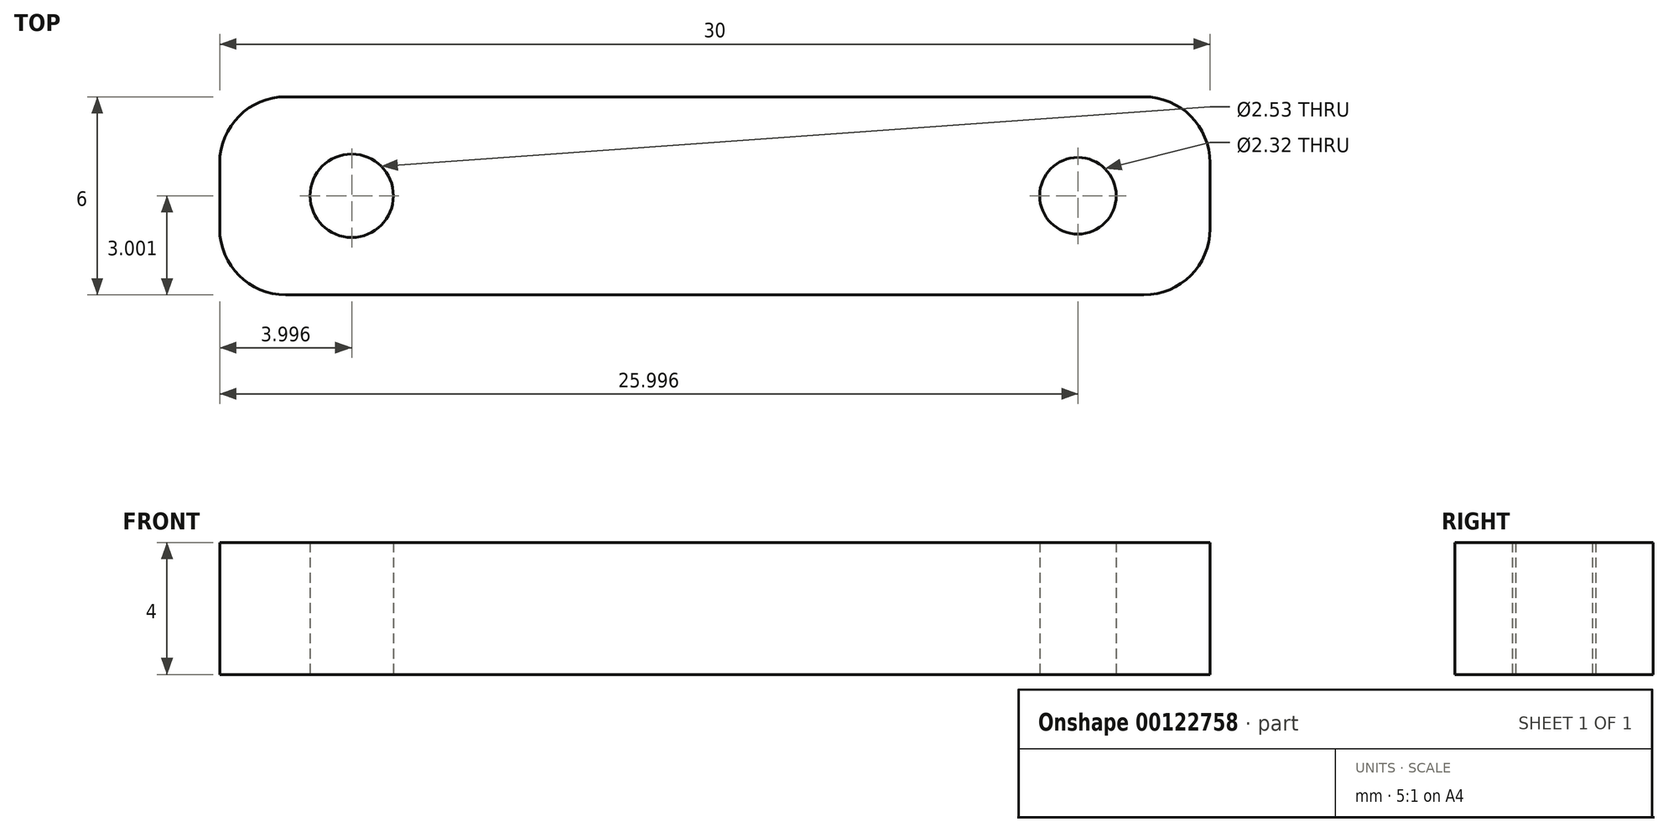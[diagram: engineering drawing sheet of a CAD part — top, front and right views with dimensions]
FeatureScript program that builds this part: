
annotation { "Feature Type Name" : "Feature", "Feature Type Description" : "" }
export const myFeature = defineFeature(function(context is Context, id is Id, definition is map)
    precondition{}
    {
        {
            var Q0;
            Q0=qCreatedBy(makeId("Top.planeOp"),FACE);
            var sketch = newSketch(context, id + "F0", { "sketchPlane" : qUnion([Q0])});
            skLineSegment(sketch, "E0.bottom", {"start": v(-1.74, 5.3) * mm, "end": v(24.26, 5.3) * mm});
            skLineSegment(sketch, "E0.top", {"start": v(-1.74, -0.7) * mm, "end": v(24.26, -0.7) * mm});
            skLineSegment(sketch, "E0.left", {"start": v(-3.74, 3.3) * mm, "end": v(-3.74, 1.3) * mm});
            skLineSegment(sketch, "E0.right", {"start": v(26.26, 3.3) * mm, "end": v(26.26, 1.3) * mm});
            skPoint(sketch, "E1.visualSharp", {"position": v(-3.74, 5.3) * mm});
            skArc(sketch, "E1.filletArc", {"start": v(-1.74, 5.3) * mm, "mid": v(-3.16, 4.7) * mm, "end": v(-3.74, 3.3) * mm});
            skPoint(sketch, "E2.visualSharp", {"position": v(-3.74, -0.7) * mm});
            skArc(sketch, "E2.filletArc", {"start": v(-3.74, 1.3) * mm, "mid": v(-3.16, -0.12) * mm, "end": v(-1.74, -0.7) * mm});
            skPoint(sketch, "E3.visualSharp", {"position": v(26.26, 5.3) * mm});
            skArc(sketch, "E3.filletArc", {"start": v(26.26, 3.3) * mm, "mid": v(25.67, 4.7) * mm, "end": v(24.26, 5.3) * mm});
            skPoint(sketch, "E4.visualSharp", {"position": v(26.26, -0.7) * mm});
            skArc(sketch, "E4.filletArc", {"start": v(24.26, -0.7) * mm, "mid": v(25.67, -0.12) * mm, "end": v(26.26, 1.3) * mm});
            skCircle(sketch, "E5", {"center": v(0.26, 2.3) * mm, "radius": 1.26 * mm});
            skCircle(sketch, "E6", {"center": v(22.26, 2.3) * mm, "radius": 1.16 * mm});
            skSolve(sketch);
        }
        {
            var Q0;
            Q0=makeQuery(id+"F0.imprint","IMPRINT",FACE,{"disambiguationData":[TD([[makeQuery(id+"F0.imprint","IMPRINT",EDGE,{"derivedFrom":sQuery(id+"F0.wireOp",EDGE,"E0.bottom")}),-1.0]])]});
            extrude(context, id + "F1", {"entities" : qUnion([Q0]), "depth" : 4 * mm});
        }
    });
